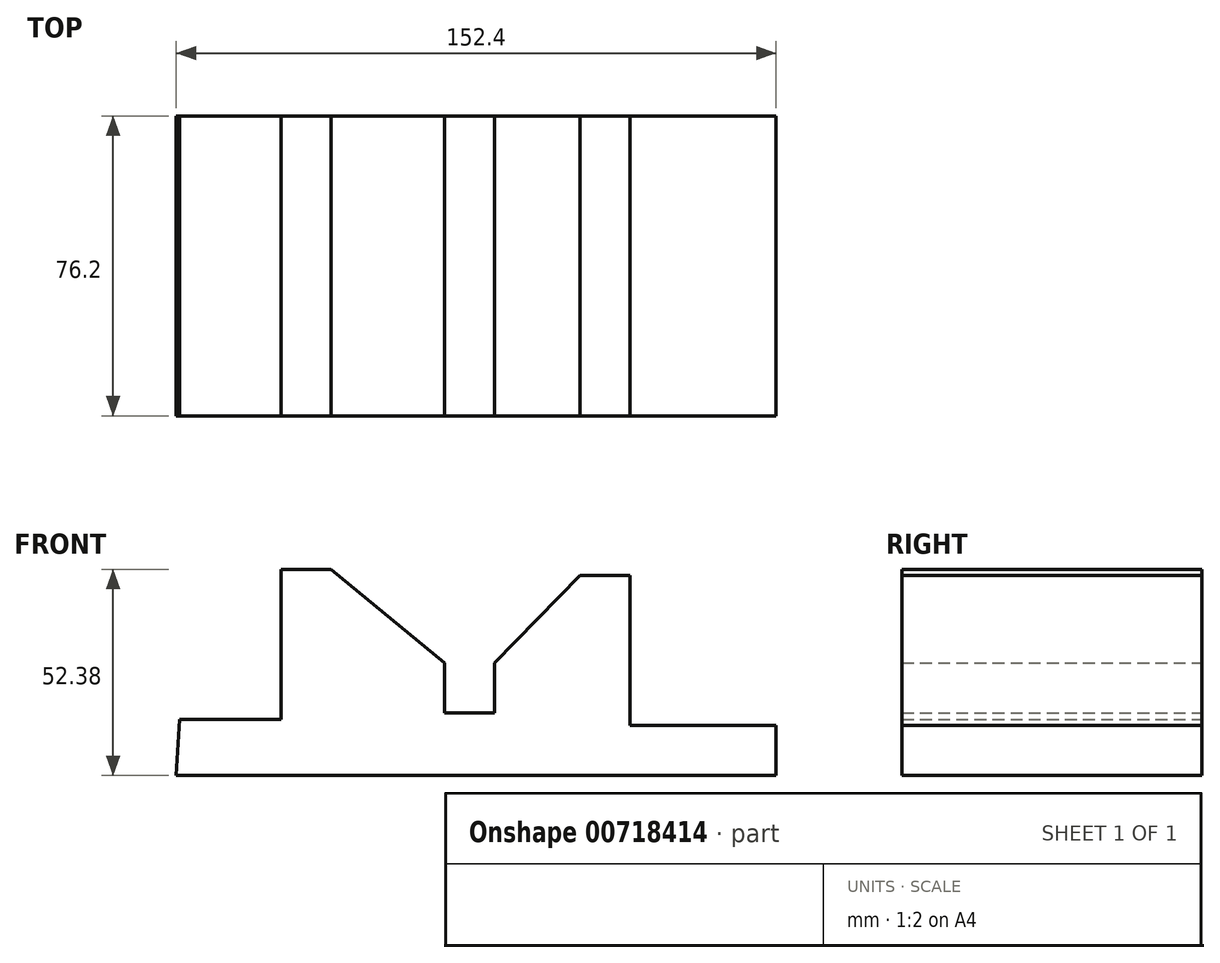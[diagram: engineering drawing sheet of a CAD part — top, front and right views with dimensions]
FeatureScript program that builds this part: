
annotation { "Feature Type Name" : "Feature", "Feature Type Description" : "" }
export const myFeature = defineFeature(function(context is Context, id is Id, definition is map)
    precondition{}
    {
        {
            var Q0;
            Q0=qCreatedBy(makeId("Front.planeOp"),FACE);
            var sketch = newSketch(context, id + "F0", { "sketchPlane" : qUnion([Q0])});
            skLineSegment(sketch, "E0", {"start": v(-68.2, -80.31) * mm, "end": v(84.2, -80.31) * mm});
            skLineSegment(sketch, "E1", {"start": v(84.2, -80.31) * mm, "end": v(84.2, -67.61) * mm});
            skLineSegment(sketch, "E2", {"start": v(84.2, -67.61) * mm, "end": v(47.12, -67.61) * mm});
            skLineSegment(sketch, "E3", {"start": v(47.12, -67.61) * mm, "end": v(47.12, -29.51) * mm});
            skLineSegment(sketch, "E4", {"start": v(47.12, -29.51) * mm, "end": v(34.42, -29.51) * mm});
            skLineSegment(sketch, "E5", {"start": v(34.42, -29.51) * mm, "end": v(12.7, -51.74) * mm});
            skLineSegment(sketch, "E6", {"start": v(12.7, -51.74) * mm, "end": v(12.7, -64.44) * mm});
            skLineSegment(sketch, "E7", {"start": v(12.7, -64.44) * mm, "end": v(0, -64.44) * mm});
            skLineSegment(sketch, "E8", {"start": v(0, -64.44) * mm, "end": v(0, -51.74) * mm});
            skLineSegment(sketch, "E9", {"start": v(0, -51.74) * mm, "end": v(-28.8, -27.93) * mm});
            skLineSegment(sketch, "E10", {"start": v(-28.8, -27.93) * mm, "end": v(-41.5, -27.93) * mm});
            skLineSegment(sketch, "E11", {"start": v(-41.5, -27.93) * mm, "end": v(-41.5, -66.03) * mm});
            skLineSegment(sketch, "E12", {"start": v(-41.5, -66.03) * mm, "end": v(-67.32, -66.03) * mm});
            skLineSegment(sketch, "E13", {"start": v(-67.32, -66.03) * mm, "end": v(-68.2, -80.31) * mm});
            skSolve(sketch);
        }
        {
            var Q0;
            Q0=makeQuery(id+"F0.imprint","IMPRINT",FACE,{"disambiguationData":[TD([[makeQuery(id+"F0.imprint","IMPRINT",EDGE,{"derivedFrom":sQuery(id+"F0.wireOp",EDGE,"E0")}),1.0]])]});
            extrude(context, id + "F1", {"entities" : qUnion([Q0]), "depth" : 76.2 * mm, "offsetDistance" : 25.4 * mm});
        }
    });
